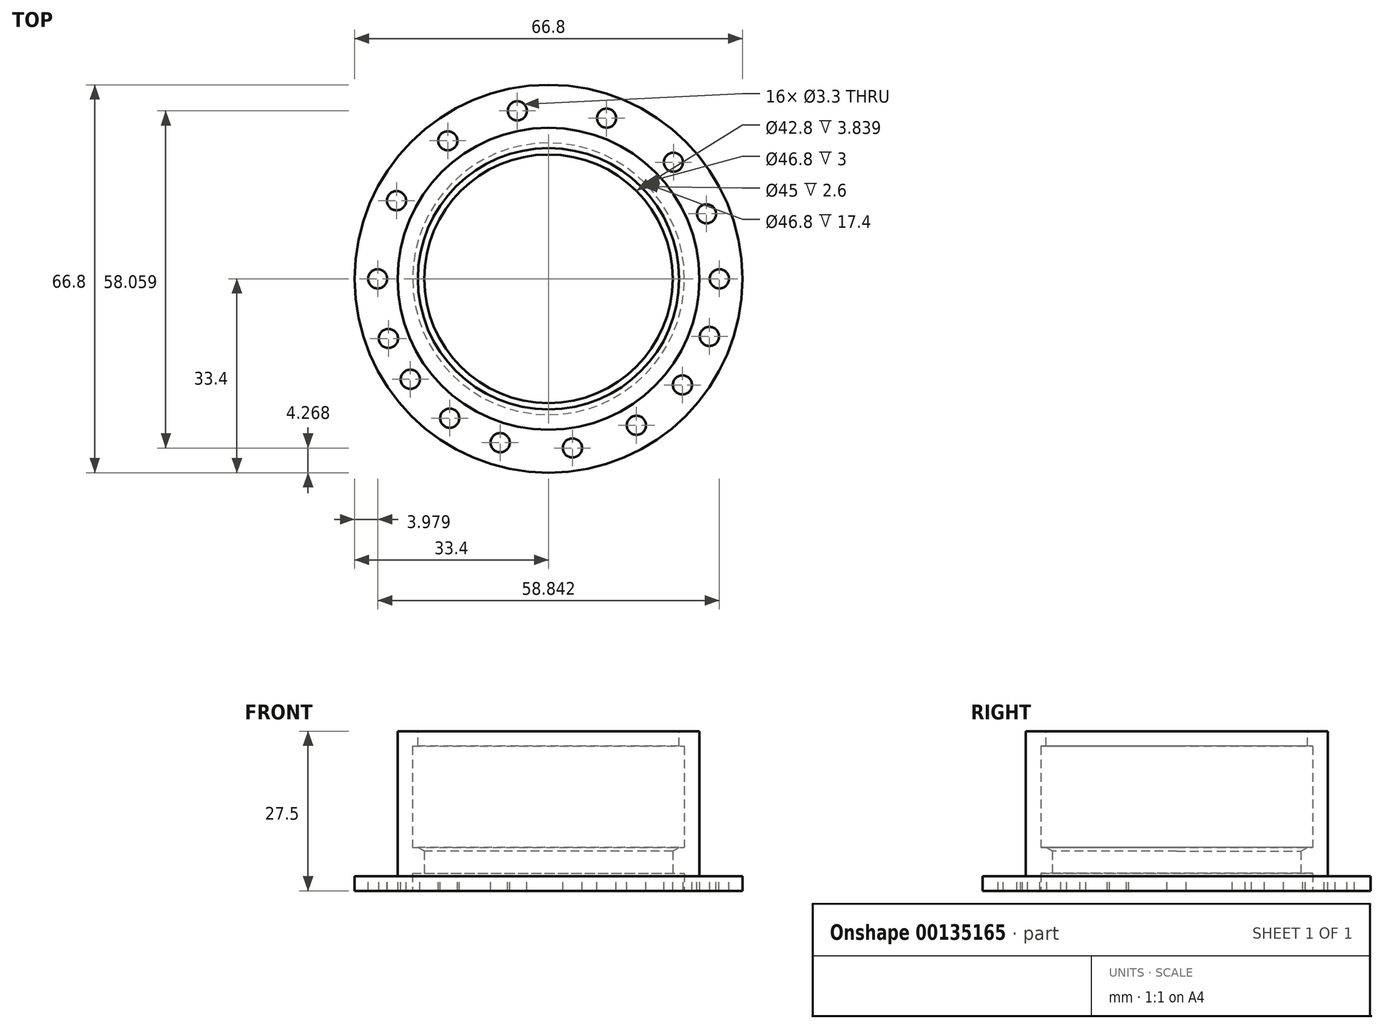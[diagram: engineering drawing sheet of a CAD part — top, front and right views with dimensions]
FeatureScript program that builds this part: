
annotation { "Feature Type Name" : "Feature", "Feature Type Description" : "" }
export const myFeature = defineFeature(function(context is Context, id is Id, definition is map)
    precondition{}
    {
        {
            var Q0;
            Q0=qCreatedBy(makeId("Right.planeOp"),FACE);
            var sketch = newSketch(context, id + "F0", { "sketchPlane" : qUnion([Q0])});
            skLineSegment(sketch, "E0", {"start": v(0, 0) * mm, "end": v(-26, 0) * mm});
            skLineSegment(sketch, "E1", {"start": v(-26, 0) * mm, "end": v(-26, -25) * mm});
            skLineSegment(sketch, "E2", {"start": v(-26, -25) * mm, "end": v(-33.4, -25) * mm});
            skLineSegment(sketch, "E3", {"start": v(-33.4, -25) * mm, "end": v(-33.4, -27.5) * mm});
            skLineSegment(sketch, "E4", {"start": v(-33.4, -27.5) * mm, "end": v(-23.4, -27.5) * mm});
            skLineSegment(sketch, "E5", {"start": v(-23.4, -27.5) * mm, "end": v(-23.4, -24.5) * mm});
            skLineSegment(sketch, "E6", {"start": v(-23.4, -24.5) * mm, "end": v(-21.4, -24.5) * mm});
            skLineSegment(sketch, "E7", {"start": v(-21.4, -24.5) * mm, "end": v(-21.4, -20) * mm});
            skLineSegment(sketch, "E8", {"start": v(-21.4, -20) * mm, "end": v(-23.4, -20) * mm});
            skLineSegment(sketch, "E9", {"start": v(-23.4, -20) * mm, "end": v(-23.4, -2.6) * mm});
            skLineSegment(sketch, "E10", {"start": v(-23.4, -2.6) * mm, "end": v(0, -2.6) * mm});
            skLineSegment(sketch, "E11", {"start": v(0, -2.6) * mm, "end": v(0, 0) * mm});
            skSolve(sketch);
        }
        {
            var Q0;
            Q0=makeQuery(id+"F0.imprint","IMPRINT",FACE,{"disambiguationData":[TD([[makeQuery(id+"F0.imprint","IMPRINT",EDGE,{"derivedFrom":sQuery(id+"F0.wireOp",EDGE,"E0")}),1.0]])]});
            var Q1;
            Q1=sQuery(id+"F0.wireOp",EDGE,"E11");
            revolve(context, id + "F1", {"entities" : qUnion([Q0]), "axis" : qUnion([Q1]), "revolveType" : RevolveType.FULL});
        }
        {
            var Q0;
            Q0=makeQuery(id+"F1.opRevolve","SWEPT_FACE",FACE,{"disambiguationData":[OSD([sQuery(id+"F0.wireOp",EDGE,"E0")])]});
            var sketch = newSketch(context, id + "F2", { "sketchPlane" : qUnion([Q0])});
            skCircle(sketch, "E12", {"center": v(0, 0) * mm, "radius": 22.08 * mm});
            skSolve(sketch);
        }
        {
            var Q0;
            Q0=sQuery(id+"F2.wireOp",VERTEX,"E12.center");
            var Q1;
            Q1=makeQuery(id+"F1.opRevolve","SWEPT_BODY",BODY,{"disambiguationData":[OSD([sQuery(id+"F0.wireOp",EDGE,"E0"),sQuery(id+"F0.wireOp",EDGE,"E1"),sQuery(id+"F0.wireOp",EDGE,"E2"),sQuery(id+"F0.wireOp",EDGE,"E3"),sQuery(id+"F0.wireOp",EDGE,"E4"),sQuery(id+"F0.wireOp",EDGE,"E5"),sQuery(id+"F0.wireOp",EDGE,"E6"),sQuery(id+"F0.wireOp",EDGE,"E7"),sQuery(id+"F0.wireOp",EDGE,"E8"),sQuery(id+"F0.wireOp",EDGE,"E9"),sQuery(id+"F0.wireOp",EDGE,"E10"),sQuery(id+"F0.wireOp",EDGE,"E11")])]});
            hole(context, id + "F3", {"style" : HoleStyle.SIMPLE, "endStyle" : HoleEndStyle.BLIND, "holeDiameter" : 45 * mm, "holeDepth" : 20 * mm, "locations" : qUnion([Q0]), "scope" : qUnion([Q1])});
        }
        {
            var Q0;
            Q0=makeQuery(id+"F1.opRevolve","SWEPT_FACE",FACE,{"disambiguationData":[OSD([sQuery(id+"F0.wireOp",EDGE,"E2")])]});
            var sketch = newSketch(context, id + "F4", { "sketchPlane" : qUnion([Q0])});
            skCircle(sketch, "E13", {"center": v(0, 0) * mm, "radius": 29.42 * mm});
            skPoint(sketch, "E14", {"position": v(-26.17, 13.45) * mm});
            skPoint(sketch, "E15", {"position": v(-17.34, 23.77) * mm});
            skPoint(sketch, "E16", {"position": v(-5.37, 28.93) * mm});
            skPoint(sketch, "E17", {"position": v(10, 27.67) * mm});
            skPoint(sketch, "E18", {"position": v(21.5, 20.08) * mm});
            skPoint(sketch, "E19", {"position": v(27.2, 11.2) * mm});
            skPoint(sketch, "E20", {"position": v(29.42, 0) * mm});
            skPoint(sketch, "E21", {"position": v(27.7, -9.92) * mm});
            skPoint(sketch, "E22", {"position": v(23.06, -18.28) * mm});
            skPoint(sketch, "E23", {"position": v(15.14, -25.23) * mm});
            skPoint(sketch, "E24", {"position": v(4.11, -29.13) * mm});
            skPoint(sketch, "E25", {"position": v(-8.32, -28.22) * mm});
            skPoint(sketch, "E26", {"position": v(-17.01, -24) * mm});
            skPoint(sketch, "E27", {"position": v(-23.8, -17.3) * mm});
            skPoint(sketch, "E28", {"position": v(-27.57, -10.27) * mm});
            skPoint(sketch, "E29", {"position": v(-29.42, 0) * mm});
            skSolve(sketch);
        }
        {
            var Q0;
            Q0=sQuery(id+"F4.wireOp",VERTEX,"E14");
            var Q1;
            Q1=sQuery(id+"F4.wireOp",VERTEX,"E15");
            var Q2;
            Q2=sQuery(id+"F4.wireOp",VERTEX,"E16");
            var Q3;
            Q3=sQuery(id+"F4.wireOp",VERTEX,"E17");
            var Q4;
            Q4=sQuery(id+"F4.wireOp",VERTEX,"E18");
            var Q5;
            Q5=sQuery(id+"F4.wireOp",VERTEX,"E19");
            var Q6;
            Q6=sQuery(id+"F4.wireOp",VERTEX,"E20");
            var Q7;
            Q7=sQuery(id+"F4.wireOp",VERTEX,"E21");
            var Q8;
            Q8=sQuery(id+"F4.wireOp",VERTEX,"E22");
            var Q9;
            Q9=sQuery(id+"F4.wireOp",VERTEX,"E23");
            var Q10;
            Q10=sQuery(id+"F4.wireOp",VERTEX,"E24");
            var Q11;
            Q11=sQuery(id+"F4.wireOp",VERTEX,"E25");
            var Q12;
            Q12=sQuery(id+"F4.wireOp",VERTEX,"E26");
            var Q13;
            Q13=sQuery(id+"F4.wireOp",VERTEX,"E27");
            var Q14;
            Q14=sQuery(id+"F4.wireOp",VERTEX,"E29");
            var Q15;
            Q15=sQuery(id+"F4.wireOp",VERTEX,"E28");
            var Q16;
            Q16=makeQuery(id+"F1.opRevolve","SWEPT_BODY",BODY,{"disambiguationData":[OSD([sQuery(id+"F0.wireOp",EDGE,"E0"),sQuery(id+"F0.wireOp",EDGE,"E1"),sQuery(id+"F0.wireOp",EDGE,"E2"),sQuery(id+"F0.wireOp",EDGE,"E3"),sQuery(id+"F0.wireOp",EDGE,"E4"),sQuery(id+"F0.wireOp",EDGE,"E5"),sQuery(id+"F0.wireOp",EDGE,"E6"),sQuery(id+"F0.wireOp",EDGE,"E7"),sQuery(id+"F0.wireOp",EDGE,"E8"),sQuery(id+"F0.wireOp",EDGE,"E9"),sQuery(id+"F0.wireOp",EDGE,"E10"),sQuery(id+"F0.wireOp",EDGE,"E11")])]});
            hole(context, id + "F5", {"style" : HoleStyle.SIMPLE, "endStyle" : HoleEndStyle.BLIND, "standardTappedOrClearance" : lookupTablePath({ "standard" : "ISO", "fit" : "Normal", "size" : "M3", "type" : "Clearance" }), "standardBlindInLast" : lookupTablePath({ "fit" : "Standard", "standard" : "ISO", "size" : "M3", "type" : "Clearance" }), "holeDiameter" : 3.3 * mm, "holeDepth" : 20 * mm, "locations" : qUnion([Q0, Q1, Q2, Q3, Q4, Q5, Q6, Q7, Q8, Q9, Q10, Q11, Q12, Q13, Q14, Q15]), "scope" : qUnion([Q16])});
        }
    });
